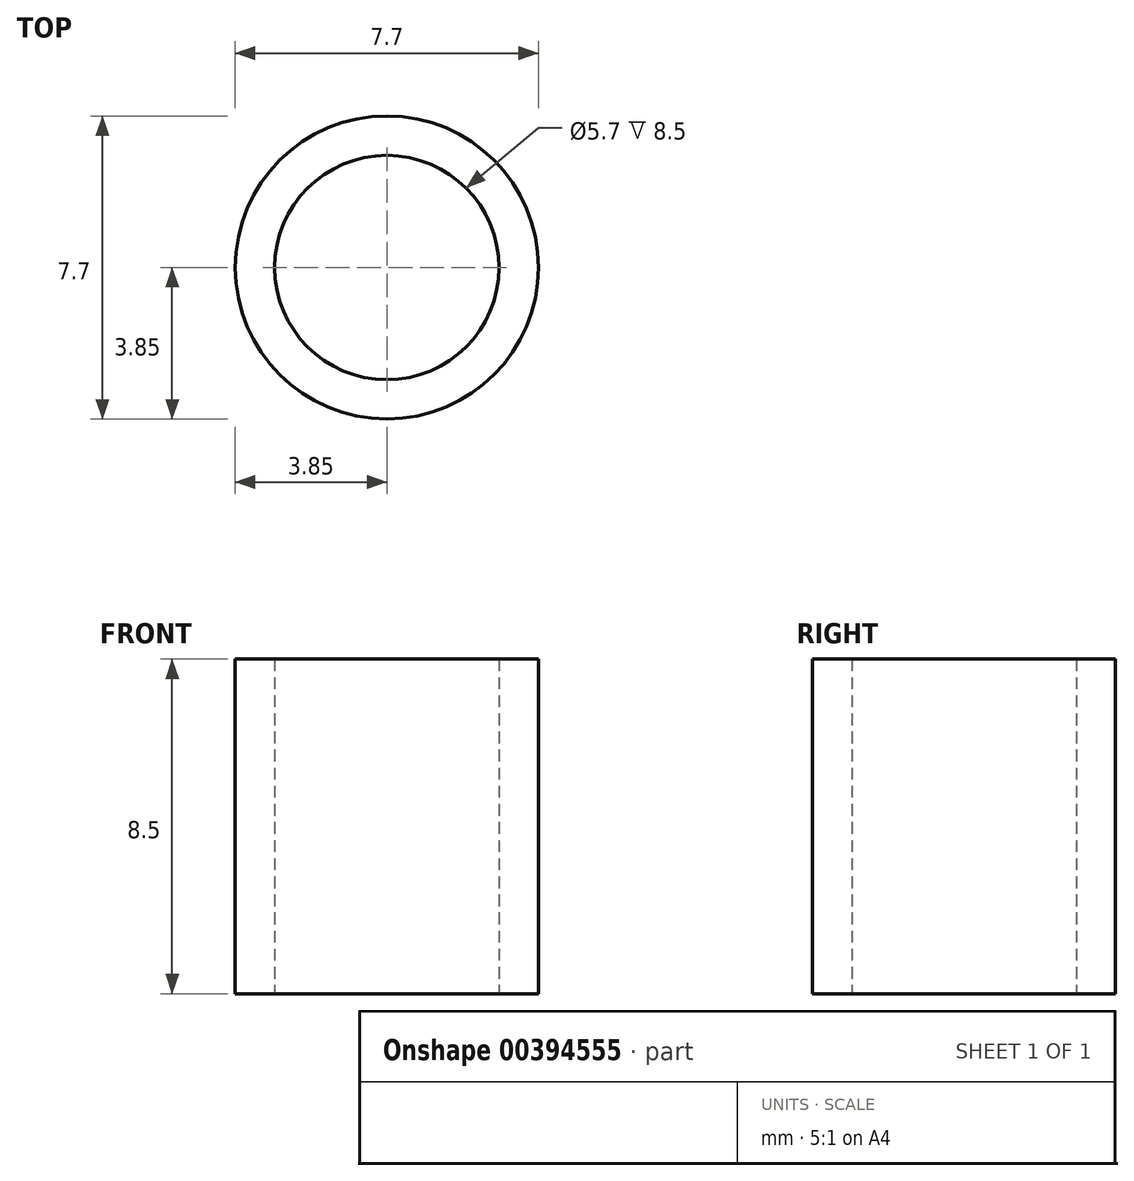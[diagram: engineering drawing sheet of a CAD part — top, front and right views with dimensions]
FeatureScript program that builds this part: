
annotation { "Feature Type Name" : "Feature", "Feature Type Description" : "" }
export const myFeature = defineFeature(function(context is Context, id is Id, definition is map)
    precondition{}
    {
        {
            var Q0;
            Q0=qCreatedBy(makeId("Top.planeOp"),FACE);
            var sketch = newSketch(context, id + "F0", { "sketchPlane" : qUnion([Q0])});
            skCircle(sketch, "E0", {"center": v(0, 0) * mm, "radius": 2.85 * mm});
            skCircle(sketch, "E1.0", {"center": v(0, 0) * mm, "radius": 3.85 * mm});
            skSolve(sketch);
        }
        {
            var Q0;
            Q0=qSketchRegion(id+"F0",true);
            extrude(context, id + "F1", {"entities" : qUnion([Q0]), "depth" : 8.5 * mm});
        }
    });
